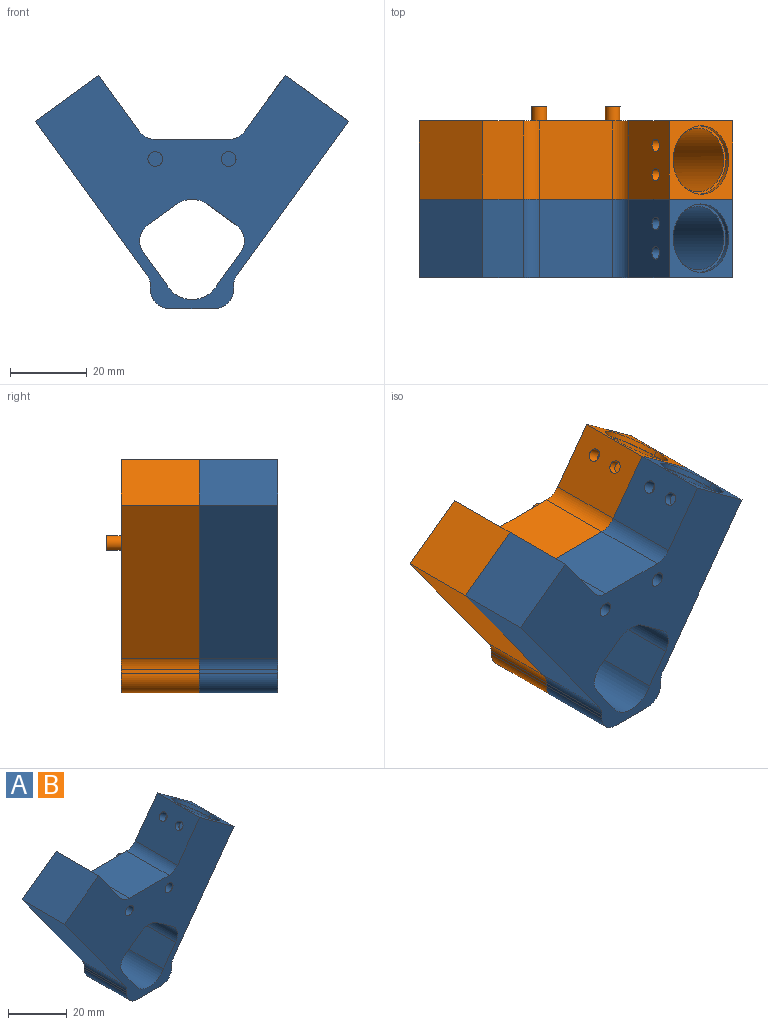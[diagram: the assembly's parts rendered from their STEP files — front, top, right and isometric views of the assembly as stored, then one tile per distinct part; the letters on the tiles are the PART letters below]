
ASSEMBLY  parts=2 mates=1
PART A: 46 faces, bbox 81.4x24.1x60.7 mm
  f0: cylinder r=8.26mm len=34.36mm, axis (0.59,0,0.81), area 1561.9mm2, adj f12,f13,f21,f22
  f1: plane 20.32x16.44mm, normal (0.59,0,0.81), area 164.6mm2, adj f2,f3,f8,f9,f10,f11
  f2: plane 39.76x28.89mm, normal (0.81,0,-0.59), area 998.7mm2, adj f1,f8,f9,f18
  f3: plane 20.32x14.59mm, normal (-0.81,0,0.59), area 349.8mm2, adj f1,f8,f9,f20,f21,f22
  f4: plane 20.32x19.07mm, normal (0,0,1), area 387.5mm2, adj f8,f9,f19,f20
  f5: plane 20.32x14.59mm, normal (0.81,0,0.59), area 366.5mm2, adj f6,f8,f9,f19
  f6: plane 20.32x16.44mm, normal (-0.59,0,0.81), area 412.9mm2, adj f5,f7,f8,f9
  f7: plane 39.76x28.89mm, normal (-0.81,0,-0.59), area 998.7mm2, adj f6,f8,f9,f17
  f8: plane 81.37x60.66mm, normal (0,-1,0), area 1945.2mm2, adj f1,f2,f3,f4,f5,f6,f7,f14
  f9: plane 81.37x60.66mm, normal (0,1,0), area 1945.2mm2, adj f1,f2,f3,f4,f5,f6,f7,f14
  f10: cylinder r=8.89mm len=17.78mm, axis (0.59,0,0.81), area 70.9mm2, adj f1,f11,f12
  f11: cylinder r=8.89mm len=1.03mm, axis (0.59,0,0.81), area 0mm2, adj f1,f10,f12
  f12: plane 17.79x14.39mm, normal (0.59,0,0.81), area 34.2mm2, adj f0,f10,f11
  f13: plane 16.52x13.37mm, normal (0.59,0,0.81), area 193.8mm2, adj f0,f36
  f14: plane 20.32x0.89mm, normal (1,0,0), area 18.1mm2, adj f8,f9,f18,f25
  f15: plane 20.32x0.89mm, normal (-1,0,0), area 18.1mm2, adj f8,f9,f17,f26
  f16: plane 20.32x11.49mm, normal (0,0,-1), area 233.5mm2, adj f8,f9,f25,f26
  f17: cylinder r=5.08mm len=20.32mm, axis (0,1,0), area 64.9mm2, adj f7,f8,f9,f15
  f18: cylinder r=5.08mm len=20.32mm, axis (0,-1,0), area 64.9mm2, adj f2,f8,f9,f14
  f19: cylinder r=5.08mm len=20.32mm, axis (0,1,0), area 97.3mm2, adj f4,f5,f8,f9
  f20: cylinder r=5.08mm len=20.32mm, axis (0,-1,0), area 97.3mm2, adj f3,f4,f8,f9
  f21: cylinder r=1.63mm len=4.31mm, axis (-0.81,0,0.59), area 29.1mm2, adj f0,f3
  f22: cylinder r=1.63mm len=4.31mm, axis (-0.81,0,0.59), area 29.1mm2, adj f0,f3
  f23: cylinder r=1.91mm len=7.62mm, axis (0.59,0,0.81), area 79.6mm2, adj f31,f37
  f24: cylinder r=7.62mm len=20.32mm, axis (0,1,0), area 335.9mm2, adj f8,f9,f28,f29
  f25: cylinder r=5.08mm len=20.32mm, axis (0,-1,0), area 162.1mm2, adj f8,f9,f14,f16
  f26: cylinder r=5.08mm len=20.32mm, axis (0,1,0), area 162.1mm2, adj f8,f9,f15,f16
  f27: plane 20.32x7.81mm, normal (0.59,0,-0.81), area 196.1mm2, adj f8,f9,f32,f35
  f28: plane 20.32x8.12mm, normal (0.81,0,0.59), area 204mm2, adj f8,f9,f24,f32
  f29: plane 20.32x8.12mm, normal (-0.81,0,0.59), area 204mm2, adj f8,f9,f24,f33
  f30: plane 20.32x1.44mm, normal (0,0,-1), area 29.3mm2, adj f8,f9,f34,f35
  f31: plane 20.32x7.81mm, normal (-0.59,0,-0.81), area 184.7mm2, adj f8,f9,f23,f33,f34
  f32: cylinder r=5.08mm len=20.32mm, axis (0,1,0), area 162.1mm2, adj f8,f9,f27,f28
  f33: cylinder r=5.08mm len=20.32mm, axis (0,1,0), area 162.1mm2, adj f8,f9,f29,f31
  f34: cylinder r=5.08mm len=20.32mm, axis (0,1,0), area 64.9mm2, adj f8,f9,f30,f31
  f35: cylinder r=5.08mm len=20.32mm, axis (0,1,0), area 64.9mm2, adj f8,f9,f27,f30
  f36: cylinder r=2.54mm len=5.08mm, axis (0.59,0,0.81), area 10.1mm2, adj f13,f37
  f37: plane 5.08x4.11mm, normal (0.59,0,0.81), area 8.9mm2, adj f23,f36
  f38: cylinder r=1.91mm len=3.81mm, axis (0,-1,0), area 45.6mm2, adj f8,f39
  f39: plane 3.81x3.81mm, normal (0,-1,0), area 11.4mm2, adj f38
  f40: cylinder r=1.91mm len=3.81mm, axis (0,-1,0), area 45.6mm2, adj f8,f41
  f41: plane 3.81x3.81mm, normal (0,-1,0), area 11.4mm2, adj f40
  f42: cylinder r=1.91mm len=3.81mm, axis (0,-1,0), area 45.6mm2, adj f9,f43
  f43: plane 3.81x3.81mm, normal (0,1,0), area 11.4mm2, adj f42
  f44: cylinder r=1.91mm len=3.81mm, axis (0,-1,0), area 45.6mm2, adj f9,f45
  f45: plane 3.81x3.81mm, normal (0,1,0), area 11.4mm2, adj f44
PART B: same geometry as A
PLACE A t=(-25.92,12.77,7.65)mm
PLACE B t=(-25.92,33.09,7.65)mm
MATE fastened A.f38 <-> B.f38  axis (0,1,0) through (-16.38,16.58,15.08)mm
